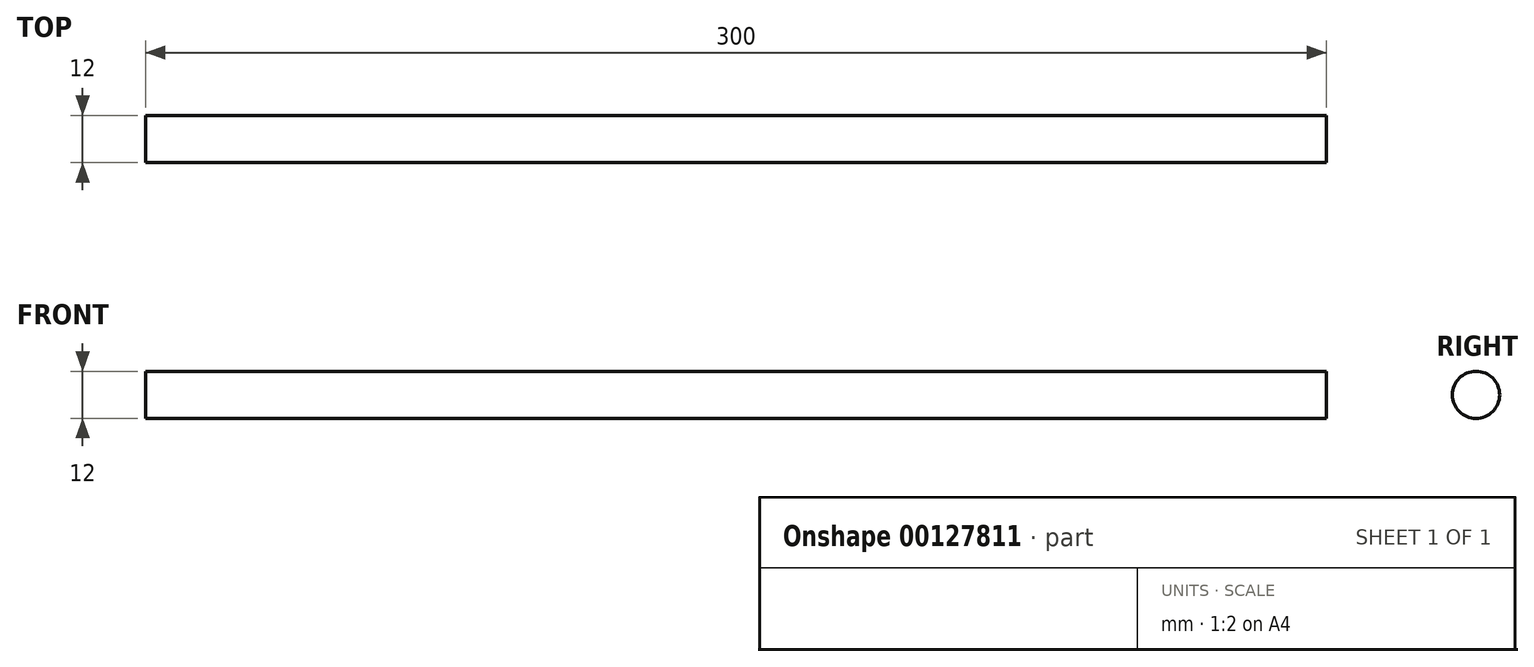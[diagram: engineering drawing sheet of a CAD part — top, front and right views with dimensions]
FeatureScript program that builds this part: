
annotation { "Feature Type Name" : "Feature", "Feature Type Description" : "" }
export const myFeature = defineFeature(function(context is Context, id is Id, definition is map)
    precondition{}
    {
        {
            var Q0;
            Q0=qCreatedBy(makeId("Right.planeOp"),FACE);
            var sketch = newSketch(context, id + "F0", { "sketchPlane" : qUnion([Q0])});
            skCircle(sketch, "E0", {"center": v(0, 0) * mm, "radius": 6 * mm});
            skSolve(sketch);
        }
        {
            var Q0;
            Q0=qSketchRegion(id+"F0",true);
            extrude(context, id + "F1", {"entities" : qUnion([Q0]), "endBound" : BoundingType.SYMMETRIC, "depth" : 300 * mm});
        }
    });
